# Revit family: E-3003
name_source: partatom
category: Plumbing Fixtures
revit_build: Autodesk Revit 2014 (Build: 20130308_1515(x64)
units: mm (PartAtom-declared; Revit-internal decimal feet)

## types (1)
- E-3003
    Brass Chromed = Brass Chromed
    CW Connection = Yes
    Description = Nuva Single Control Wall Mounted With Mushroom Drain Without Overflow
    Documentation = http://www.helvex.com.mx
    Features = Ceramic Cartridge
    HW Connection = Yes
    Inlet Threads = 5/8" Brass Tube
    Installation Adjustment = 9,52 mm (3/8") Max. Range
    Instructive = http://www.helvex.com.mx
    Manufacturer = Helvex
    Max. Working Pressure = 85.3 psi
    Min. Working Pressure = 11.4 psi
    Model = E-3003
    Niquel Duravex = Niquel Duravex
    Satin = Satin
    Total Length = 8"
    Total Width = 5"
    Type Comments = Single Control Wall Mounted Lavatory Faucet
    URL = http://www.helvex.com.mx

## geometry (parser evidence)
native form markers: Sweep x1
no freeform markers — native parametric forms only
